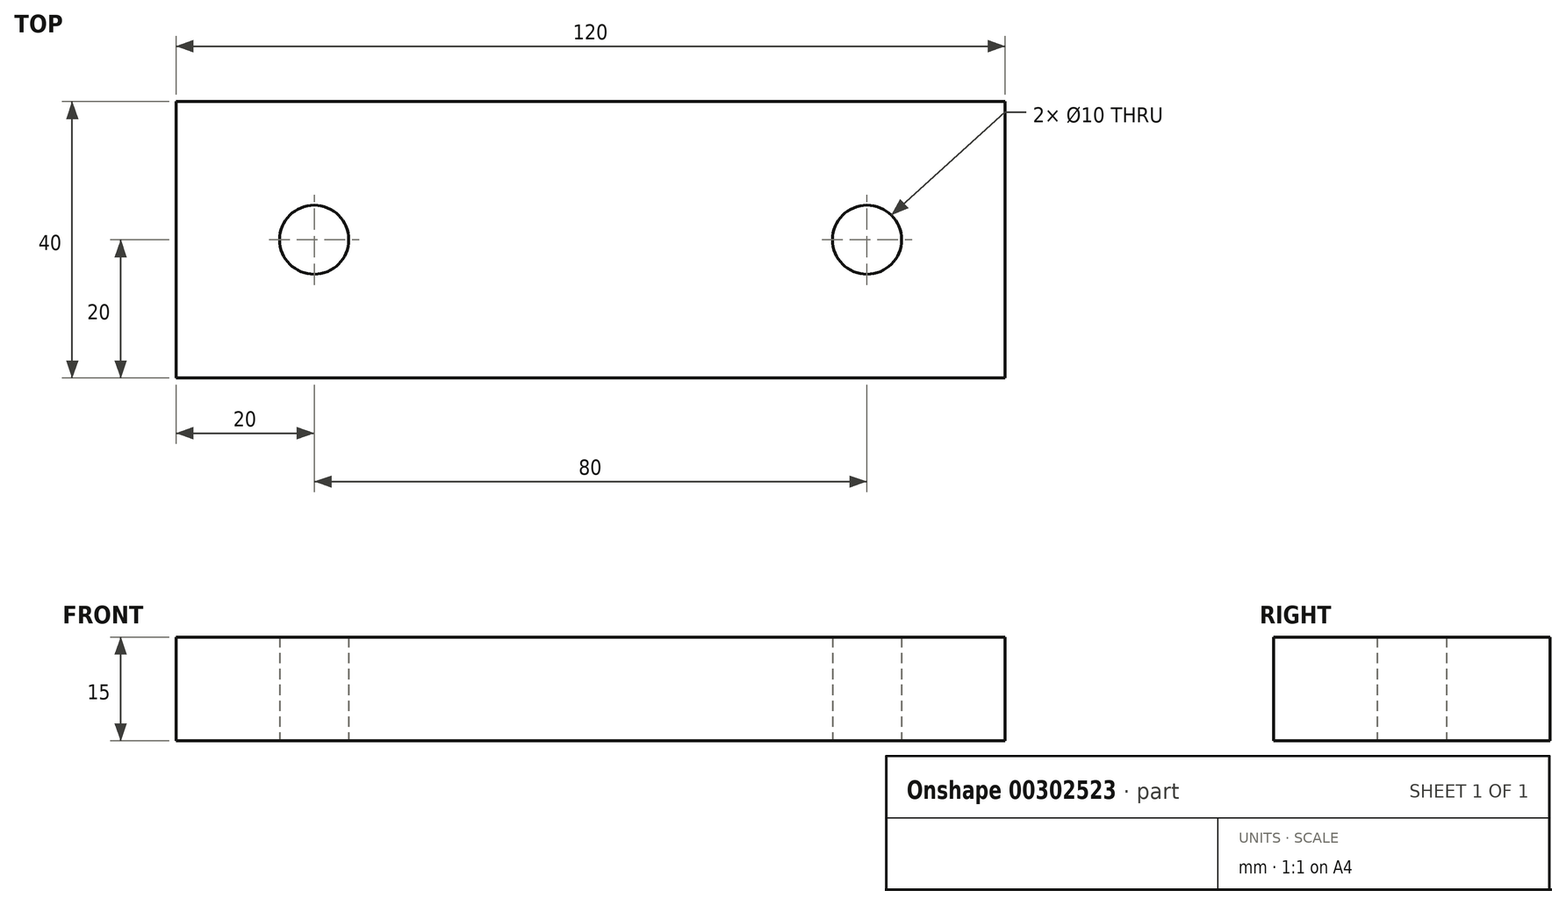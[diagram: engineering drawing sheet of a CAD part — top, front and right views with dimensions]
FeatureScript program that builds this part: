
annotation { "Feature Type Name" : "Feature", "Feature Type Description" : "" }
export const myFeature = defineFeature(function(context is Context, id is Id, definition is map)
    precondition{}
    {
        {
            var Q0;
            Q0=qCreatedBy(makeId("Top.planeOp"),FACE);
            var sketch = newSketch(context, id + "F0", { "sketchPlane" : qUnion([Q0])});
            skLineSegment(sketch, "E0", {"start": v(0, 0) * mm, "end": v(0, 40) * mm});
            skLineSegment(sketch, "E1", {"start": v(0, 40) * mm, "end": v(120, 40) * mm});
            skLineSegment(sketch, "E2", {"start": v(120, 40) * mm, "end": v(120, 0) * mm});
            skLineSegment(sketch, "E3", {"start": v(120, 0) * mm, "end": v(0, 0) * mm});
            skCircle(sketch, "E4", {"center": v(20, 20) * mm, "radius": 5 * mm});
            skCircle(sketch, "E5", {"center": v(100, 20) * mm, "radius": 5 * mm});
            skPoint(sketch, "E6", {"position": v(0, 20) * mm});
            skSolve(sketch);
        }
        {
            var Q0;
            Q0 = qSketchRegion(id + "F0", true);
            extrude(context, id + "F1", {"entities" : qUnion([Q0]), "depth" : 15 * mm});
        }
    });
